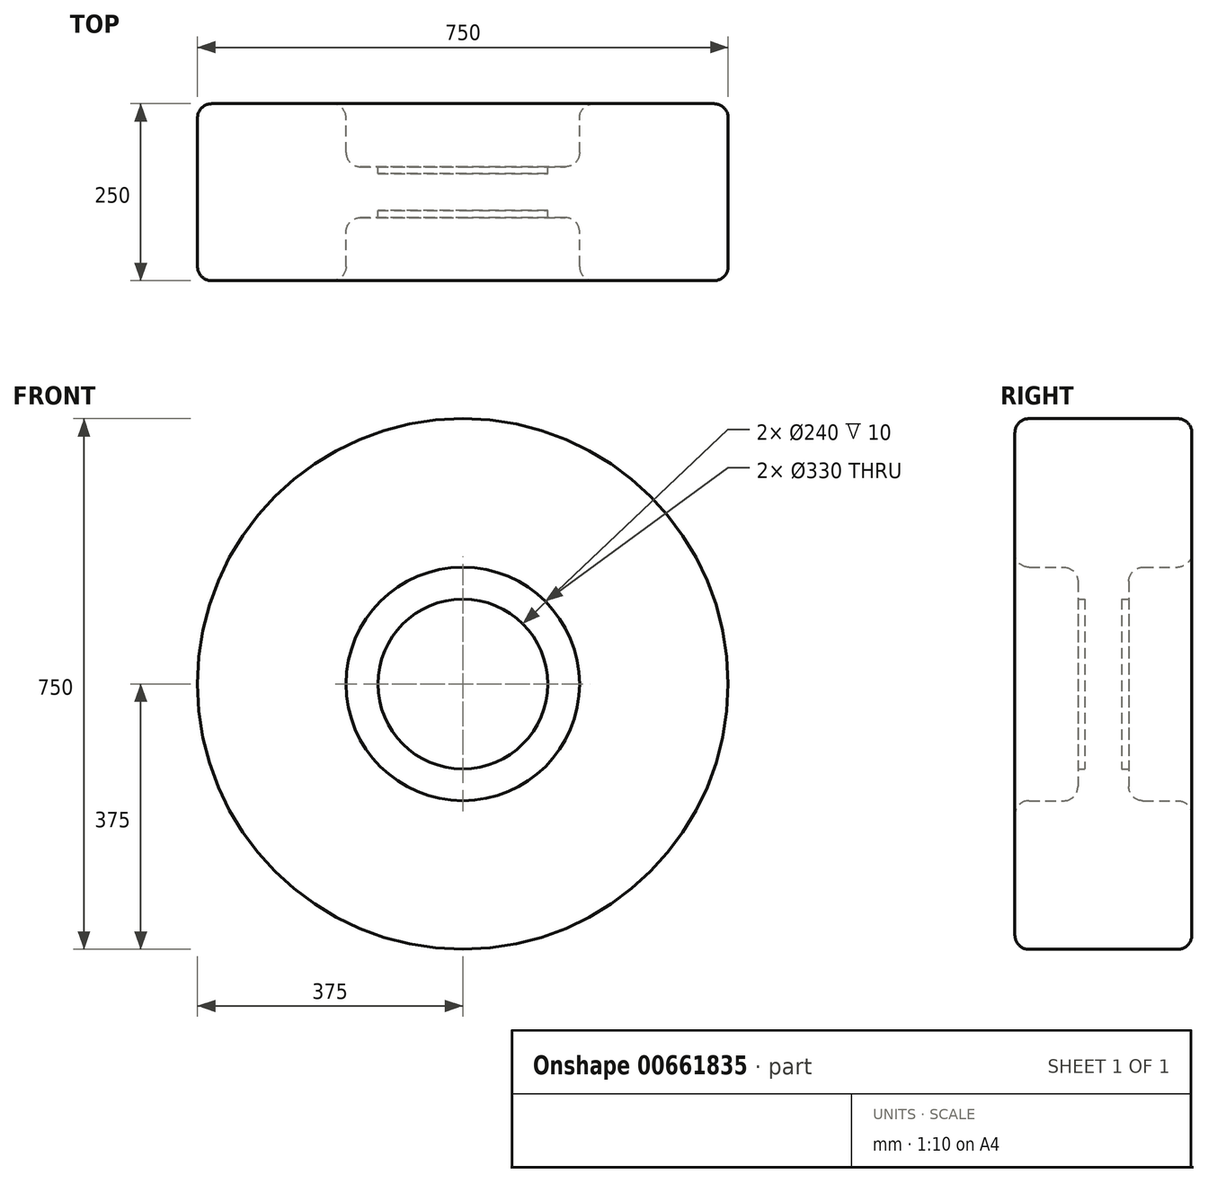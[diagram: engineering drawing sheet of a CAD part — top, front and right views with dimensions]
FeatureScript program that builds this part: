
annotation { "Feature Type Name" : "Feature", "Feature Type Description" : "" }
export const myFeature = defineFeature(function(context is Context, id is Id, definition is map)
    precondition{}
    {
        {
            var Q0;
            Q0=qCreatedBy(makeId("Top.planeOp"),FACE);
            var sketch = newSketch(context, id + "F0", { "sketchPlane" : qUnion([Q0])});
            skLineSegment(sketch, "E0", {"start": v(0, -26) * mm, "end": v(120, -26) * mm});
            skLineSegment(sketch, "E1", {"start": v(120, -26) * mm, "end": v(120, -36) * mm});
            skLineSegment(sketch, "E2", {"start": v(120, -36) * mm, "end": v(145, -36) * mm});
            skLineSegment(sketch, "E3", {"start": v(165, -56) * mm, "end": v(165, -105) * mm});
            skLineSegment(sketch, "E4", {"start": v(185, -125) * mm, "end": v(355, -125) * mm});
            skLineSegment(sketch, "E5", {"start": v(375, -105) * mm, "end": v(375, 105) * mm});
            skLineSegment(sketch, "E6", {"start": v(355, 125) * mm, "end": v(185, 125) * mm});
            skLineSegment(sketch, "E7", {"start": v(165, 105) * mm, "end": v(165, 56) * mm});
            skLineSegment(sketch, "E8", {"start": v(0, 26) * mm, "end": v(0, -26) * mm});
            skLineSegment(sketch, "E9", {"start": v(0, 26) * mm, "end": v(120, 26) * mm});
            skLineSegment(sketch, "E10", {"start": v(120, 26) * mm, "end": v(120, 36) * mm});
            skLineSegment(sketch, "E11", {"start": v(120, 36) * mm, "end": v(145, 36) * mm});
            skPoint(sketch, "E12.visualSharp", {"position": v(165, 125) * mm});
            skArc(sketch, "E12.filletArc", {"start": v(185, 125) * mm, "mid": v(170.86, 119.14) * mm, "end": v(165, 105) * mm});
            skPoint(sketch, "E13.visualSharp", {"position": v(375, 125) * mm});
            skArc(sketch, "E13.filletArc", {"start": v(375, 105) * mm, "mid": v(369.14, 119.14) * mm, "end": v(355, 125) * mm});
            skPoint(sketch, "E14.visualSharp", {"position": v(375, -125) * mm});
            skArc(sketch, "E14.filletArc", {"start": v(355, -125) * mm, "mid": v(369.14, -119.14) * mm, "end": v(375, -105) * mm});
            skPoint(sketch, "E15.visualSharp", {"position": v(165, -125) * mm});
            skArc(sketch, "E15.filletArc", {"start": v(165, -105) * mm, "mid": v(170.86, -119.14) * mm, "end": v(185, -125) * mm});
            skPoint(sketch, "E16.visualSharp", {"position": v(165, 36) * mm});
            skArc(sketch, "E16.filletArc", {"start": v(145, 36) * mm, "mid": v(159.14, 41.86) * mm, "end": v(165, 56) * mm});
            skPoint(sketch, "E17.visualSharp", {"position": v(165, -36) * mm});
            skArc(sketch, "E17.filletArc", {"start": v(165, -56) * mm, "mid": v(159.14, -41.86) * mm, "end": v(145, -36) * mm});
            skSolve(sketch);
        }
        {
            var Q0;
            Q0=makeQuery(id+"F0.imprint","IMPRINT",FACE,{"disambiguationData":[TD([[makeQuery(id+"F0.imprint","IMPRINT",EDGE,{"derivedFrom":sQuery(id+"F0.wireOp",EDGE,"E0")}),1.0]])]});
            var Q1;
            Q1=sQuery(id+"F0.wireOp",EDGE,"E8");
            revolve(context, id + "F1", {"entities" : qUnion([Q0]), "axis" : qUnion([Q1]), "revolveType" : RevolveType.FULL});
        }
    });
